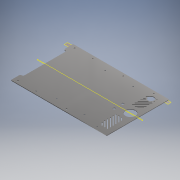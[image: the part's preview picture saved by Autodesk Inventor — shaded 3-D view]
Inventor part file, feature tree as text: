
AUTODESK INVENTOR PART (.ipt)
format: ipt  version: 2018 (Build 220112000, 112)  size: 603,648 bytes
history: native  units: mm
features: other x12, reference x11, sketch x9, extrude x8, projected_geometry x4, plane x2, fillet x1
ambient origin geometry x8: Origin, YZ Plane, XZ Plane, XY Plane, X Axis, Y Axis, Z Axis, Center Point
bodies: Volumenkörper1 (feature_tree)
feature tree (47):
  plane  "Arbeitsebene1"
  other  "Fläche1"
  other  "Eckenrundung1"
  extrude  "Extrusion1"  Depth=345.0mm
  extrude  "Extrusion2"  Depth=30.499917mm
  extrude  "Extrusion3"  Depth=2.0mm
  extrude  "Extrusion4"  Depth=10.0mm
  plane  "Arbeitsebene2"
  extrude  "Extrusion5"  Depth=10.0mm
  extrude  "Extrusion7"  Depth=10.0mm TaperAngle=0.0deg
  extrude  "Extrusion8"  Depth=10.0mm
  extrude  "Extrusion10"  Depth=10.0mm
  fillet  "Rundung1"  Radius=10.0mm
  sketch  "Skizze1"  dims[d0=0.0mm d1=345.0mm]
  reference  "Referenz1"
  other  "Grobblech1"
  sketch  "Skizze2"  dims[d2=193.499917mm d3=30.499917mm]
  projected_geometry  "Projizierte Kontur1"
  reference  "Referenz2"
  reference  "Referenz3"
  sketch  "Skizze3"  dims[d4=2.0mm d5=2.0mm]
  reference  "Referenz4"
  sketch  "Skizze4"  dims[d6=10.0mm d7=34.0mm]
  reference  "Referenz5"
  sketch  "Skizze5"  dims[d8=10.0mm d9=34.0mm]
  reference  "Referenz6"
  reference  "Referenz7"
  reference  "Referenz8"
  reference  "Referenz9"
  reference  "Referenz10"
  reference  "Referenz11"
  sketch  "Skizze6"  dims[d10=5.0mm d11=10.0mm d12=0.0mm]
  sketch  "Skizze7"  dims[d13=10.0mm d14=0.0mm d15=8.0mm]
  projected_geometry  "Projizierte Kontur2"
  sketch  "Skizze8"  dims[d16=8.0mm d17=15.0mm d18=10.0mm]
  projected_geometry  "Projizierte Kontur3"
  sketch  "Skizze9"  dims[d19=10.0mm d20=15.0mm d21=10.0mm d22=0.0mm d23=10.0mm d24=0.0mm d25=10.0mm d26=0.0mm d27=1.5mm d29=70.0mm d31=10.0mm d33=40.0mm d35=10.0mm d37=70.0mm d39=10.0mm d41=40.0mm d43=10.0mm d50=10.0mm d51=10.0mm d52=10.0mm d53=10.0mm d62=10.0mm d63=10.0mm d64=10.0mm d65=10.0mm d71=1.84mm d72=10.0mm d73=0.0mm d75=27.5mm d76=34.679864mm d77=30.0mm d78=2.0mm d79=0.0mm d80=21.5mm d83=7.5mm d85=22.697331mm d86=54.80232mm d87=2.0mm d88=0.0mm d89=2.0mm]
  projected_geometry  "Projizierte Kontur4"
  parser-record x1  (decoder bookkeeping rows leaked as tree rows — omitted from the tree; the rows remain in map.json)
  other  "Montiert.iam"
  other  "Front:1"
  other  "Boden:1"
  other  "Brenner:1"
  other  "BrennerHalter:1"
  other  "SeiteRechts:1"
  other  "SeiteLinks:1"
  other  "Definition1"
note: 1 file-system path scrubbed to <path> (originals preserved in map.json)
